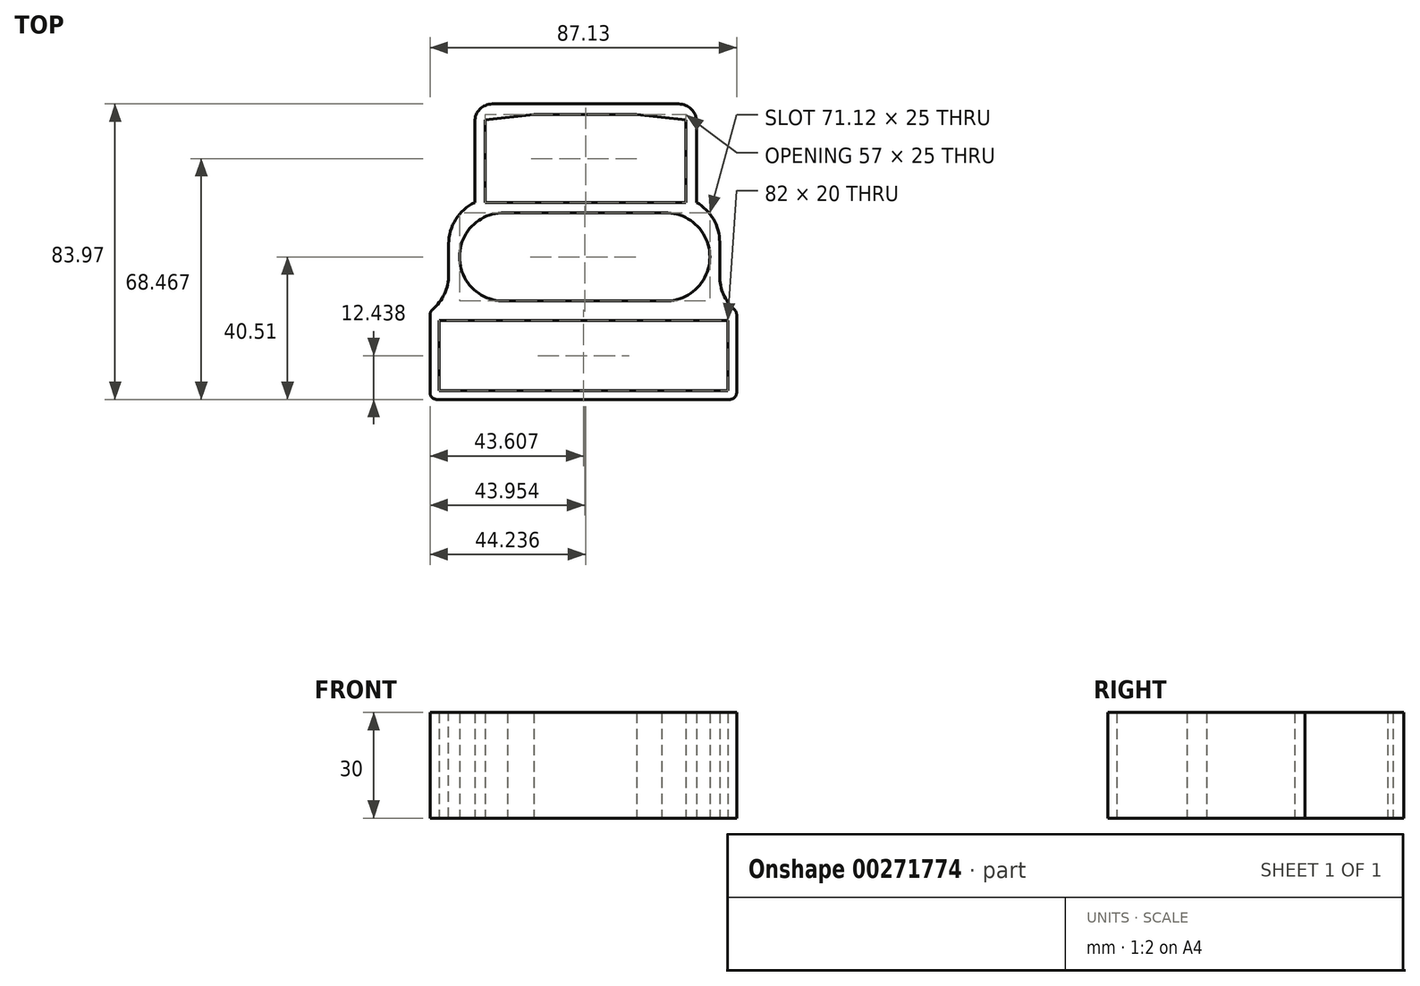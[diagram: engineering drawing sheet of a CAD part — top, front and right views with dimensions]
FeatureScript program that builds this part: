
annotation { "Feature Type Name" : "Feature", "Feature Type Description" : "" }
export const myFeature = defineFeature(function(context is Context, id is Id, definition is map)
    precondition{}
    {
        {
            var Q0;
            Q0=qCreatedBy(makeId("Top.planeOp"),FACE);
            var sketch = newSketch(context, id + "F0", { "sketchPlane" : qUnion([Q0])});
            skLineSegment(sketch, "E0.bottom", {"start": v(-35.62, 12.5) * mm, "end": v(35.38, 12.5) * mm});
            skLineSegment(sketch, "E0.top", {"start": v(-35.62, -12.5) * mm, "end": v(35.38, -12.5) * mm});
            skLineSegment(sketch, "E0.left", {"start": v(-35.62, 12.5) * mm, "end": v(-35.62, -12.5) * mm});
            skLineSegment(sketch, "E0.right", {"start": v(35.38, 12.5) * mm, "end": v(35.38, -12.5) * mm});
            skLineSegment(sketch, "E1.bottom", {"start": v(-38.8, 15.46) * mm, "end": v(38.2, 15.46) * mm});
            skLineSegment(sketch, "E1.top", {"start": v(-38.8, -15.54) * mm, "end": v(38.2, -15.54) * mm});
            skLineSegment(sketch, "E1.left", {"start": v(-38.8, 15.46) * mm, "end": v(-38.8, -15.54) * mm});
            skLineSegment(sketch, "E1.right", {"start": v(38.2, 15.46) * mm, "end": v(38.2, -15.54) * mm});
            skCircle(sketch, "E2", {"center": v(-23.15, 0) * mm, "radius": 12.55 * mm});
            skCircle(sketch, "E3", {"center": v(22.88, 0) * mm, "radius": 12.55 * mm});
            skLineSegment(sketch, "E4.bottom", {"start": v(-28.35, 15.46) * mm, "end": v(28.65, 15.46) * mm});
            skLineSegment(sketch, "E4.top", {"start": v(-28.35, 40.46) * mm, "end": v(28.65, 40.46) * mm});
            skLineSegment(sketch, "E4.left", {"start": v(-28.35, 15.46) * mm, "end": v(-28.35, 40.46) * mm});
            skLineSegment(sketch, "E4.right", {"start": v(28.65, 15.46) * mm, "end": v(28.65, 40.46) * mm});
            skLineSegment(sketch, "E5.bottom", {"start": v(-31.37, 15.46) * mm, "end": v(31.63, 15.46) * mm});
            skLineSegment(sketch, "E5.top", {"start": v(-31.37, 43.46) * mm, "end": v(31.63, 43.46) * mm});
            skLineSegment(sketch, "E5.left", {"start": v(-31.37, 15.46) * mm, "end": v(-31.37, 43.46) * mm});
            skLineSegment(sketch, "E5.right", {"start": v(31.63, 15.46) * mm, "end": v(31.63, 43.46) * mm});
            skLineSegment(sketch, "E6", {"start": v(14.6, 40.46) * mm, "end": v(28.65, 38.9) * mm});
            skLineSegment(sketch, "E7", {"start": v(-14.6, 40.46) * mm, "end": v(-28.35, 38.9) * mm});
            skLineSegment(sketch, "E8.bottom", {"start": v(-41.48, -18.07) * mm, "end": v(40.52, -18.07) * mm});
            skLineSegment(sketch, "E8.top", {"start": v(-41.48, -38.07) * mm, "end": v(40.52, -38.07) * mm});
            skLineSegment(sketch, "E8.left", {"start": v(-41.48, -18.07) * mm, "end": v(-41.48, -38.07) * mm});
            skLineSegment(sketch, "E8.right", {"start": v(40.52, -18.07) * mm, "end": v(40.52, -38.07) * mm});
            skLineSegment(sketch, "E9.bottom", {"start": v(-44.09, -15.54) * mm, "end": v(43.04, -15.54) * mm});
            skLineSegment(sketch, "E9.top", {"start": v(-44.09, -40.5) * mm, "end": v(43.04, -40.5) * mm});
            skLineSegment(sketch, "E9.left", {"start": v(-44.09, -15.54) * mm, "end": v(-44.09, -40.5) * mm});
            skLineSegment(sketch, "E9.right", {"start": v(43.04, -15.54) * mm, "end": v(43.04, -40.5) * mm});
            skSolve(sketch);
        }
        {
            var Q0;
            {var subQ0=sQuery(id+"F0.wireOp",EDGE,"E0.right");var subQ1=sQuery(id+"F0.wireOp",EDGE,"E0.bottom");var subQ2=makeQuery(id+"F0.imprint","INTERSECT",VERTEX,{"derivedFrom":[subQ1,subQ0]});Q0=makeQuery(id+"F0.imprint","IMPRINT",FACE,{"disambiguationData":[TD([[makeQuery(id+"F0.imprint","IMPRINT",EDGE,{"disambiguationData":[TD([[subQ2,1.0]])],"derivedFrom":subQ1}),-1.0]])]});}
            var Q1;
            {var subQ0=sQuery(id+"F0.wireOp",EDGE,"E0.right");var subQ1=sQuery(id+"F0.wireOp",EDGE,"E0.top");var subQ2=makeQuery(id+"F0.imprint","INTERSECT",VERTEX,{"derivedFrom":[subQ1,subQ0]});Q1=makeQuery(id+"F0.imprint","IMPRINT",FACE,{"disambiguationData":[TD([[makeQuery(id+"F0.imprint","IMPRINT",EDGE,{"disambiguationData":[TD([[subQ2,1.0]])],"derivedFrom":subQ1}),1.0]])]});}
            var Q2;
            {var subQ0=sQuery(id+"F0.wireOp",EDGE,"E0.left");var subQ1=sQuery(id+"F0.wireOp",EDGE,"E0.top");var subQ2=makeQuery(id+"F0.imprint","INTERSECT",VERTEX,{"derivedFrom":[subQ1,subQ0]});Q2=makeQuery(id+"F0.imprint","IMPRINT",FACE,{"disambiguationData":[TD([[makeQuery(id+"F0.imprint","IMPRINT",EDGE,{"disambiguationData":[TD([[subQ2,-1.0]])],"derivedFrom":subQ1}),1.0]])]});}
            var Q3;
            {var subQ0=sQuery(id+"F0.wireOp",EDGE,"E0.left");var subQ1=sQuery(id+"F0.wireOp",EDGE,"E0.bottom");var subQ2=makeQuery(id+"F0.imprint","INTERSECT",VERTEX,{"derivedFrom":[subQ1,subQ0]});Q3=makeQuery(id+"F0.imprint","IMPRINT",FACE,{"disambiguationData":[TD([[makeQuery(id+"F0.imprint","IMPRINT",EDGE,{"disambiguationData":[TD([[subQ2,-1.0]])],"derivedFrom":subQ1}),-1.0]])]});}
            var Q4;
            Q4=makeQuery(id+"F0.imprint","IMPRINT",FACE,{"disambiguationData":[TD([[makeQuery(id+"F0.imprint","IMPRINT",EDGE,{"derivedFrom":sQuery(id+"F0.wireOp",EDGE,"E1.bottom")}),-1.0]])]});
            var Q5;
            Q5=makeQuery(id+"F0.imprint","IMPRINT",FACE,{"disambiguationData":[TD([[makeQuery(id+"F0.imprint","IMPRINT",EDGE,{"derivedFrom":sQuery(id+"F0.wireOp",EDGE,"E5.top")}),-1.0]])]});
            var Q6;
            {var subQ3=sQuery(id+"F0.wireOp",EDGE,"E6");Q6=makeQuery(id+"F0.imprint","IMPRINT",FACE,{"disambiguationData":[TD([[makeQuery(id+"F0.imprint","IMPRINT",EDGE,{"derivedFrom":subQ3}),1.0]])]});}
            var Q7;
            {var subQ3=sQuery(id+"F0.wireOp",EDGE,"E7");Q7=makeQuery(id+"F0.imprint","IMPRINT",FACE,{"disambiguationData":[TD([[makeQuery(id+"F0.imprint","IMPRINT",EDGE,{"derivedFrom":subQ3}),-1.0]])]});}
            var Q8;
            Q8=makeQuery(id+"F0.imprint","IMPRINT",FACE,{"disambiguationData":[TD([[makeQuery(id+"F0.imprint","IMPRINT",EDGE,{"derivedFrom":sQuery(id+"F0.wireOp",EDGE,"E8.bottom")}),1.0]])]});
            extrude(context, id + "F1", {"entities" : qUnion([Q0, Q1, Q2, Q3, Q4, Q5, Q6, Q7, Q8]), "depth" : 30 * mm});
        }
        {
            var Q0;
            Q0=makeQuery(id+"F1.opExtrude","SWEPT_EDGE",EDGE,{"disambiguationData":[OSD([sQuery(id+"F0.wireOp",EDGE,"E1.top"),sQuery(id+"F0.wireOp",EDGE,"E1.left")])]});
            var Q1;
            Q1=makeQuery(id+"F1.opExtrude","SWEPT_EDGE",EDGE,{"disambiguationData":[OSD([sQuery(id+"F0.wireOp",EDGE,"E1.bottom"),sQuery(id+"F0.wireOp",EDGE,"E1.left")])]});
            var Q2;
            Q2=makeQuery(id+"F1.opExtrude","SWEPT_EDGE",EDGE,{"disambiguationData":[OSD([sQuery(id+"F0.wireOp",EDGE,"E1.top"),sQuery(id+"F0.wireOp",EDGE,"E1.right")])]});
            var Q3;
            Q3=makeQuery(id+"F1.opExtrude","SWEPT_EDGE",EDGE,{"disambiguationData":[OSD([sQuery(id+"F0.wireOp",EDGE,"E1.bottom"),sQuery(id+"F0.wireOp",EDGE,"E1.right")])]});
            fillet(context, id + "F2", {"entities" : qUnion([Q0, Q1, Q2, Q3]), "radius" : 13 * mm, "tangentPropagation" : true, "allowEdgeOverflow" : false});
        }
        {
            var Q0;
            Q0=makeQuery(id+"F1.opExtrude","SWEPT_EDGE",EDGE,{"disambiguationData":[OSD([sQuery(id+"F0.wireOp",EDGE,"E5.top"),sQuery(id+"F0.wireOp",EDGE,"E5.right")])]});
            var Q1;
            Q1=makeQuery(id+"F1.opExtrude","SWEPT_EDGE",EDGE,{"disambiguationData":[OSD([sQuery(id+"F0.wireOp",EDGE,"E5.top"),sQuery(id+"F0.wireOp",EDGE,"E5.left")])]});
            fillet(context, id + "F3", {"entities" : qUnion([Q0, Q1]), "radius" : 5 * mm, "tangentPropagation" : true, "allowEdgeOverflow" : false});
        }
        {
            var Q0;
            Q0=makeQuery(id+"F2.opFillet","BLEND_EDGE",EDGE,{"blendedFrom":[makeQuery(id+"F1.opExtrude","SWEPT_EDGE",EDGE,{"disambiguationData":[OSD([sQuery(id+"F0.wireOp",EDGE,"E1.left"),sQuery(id+"F0.wireOp",EDGE,"E9.bottom")])]}),makeQuery(id+"F1.opExtrude","SWEPT_FACE",FACE,{"disambiguationData":[OSD([sQuery(id+"F0.wireOp",EDGE,"E9.left")])]})],"blendedInto":[makeQuery(id+"F1.opExtrude","SWEPT_FACE",FACE,{"disambiguationData":[OSD([sQuery(id+"F0.wireOp",EDGE,"E9.left")])]})]});
            var Q1;
            Q1=makeQuery(id+"F1.opExtrude","SWEPT_EDGE",EDGE,{"disambiguationData":[OSD([sQuery(id+"F0.wireOp",EDGE,"E9.top"),sQuery(id+"F0.wireOp",EDGE,"E9.left")])]});
            var Q2;
            Q2=makeQuery(id+"F1.opExtrude","SWEPT_EDGE",EDGE,{"disambiguationData":[OSD([sQuery(id+"F0.wireOp",EDGE,"E9.top"),sQuery(id+"F0.wireOp",EDGE,"E9.right")])]});
            var Q3;
            Q3=makeQuery(id+"F2.opFillet","BLEND_EDGE",EDGE,{"blendedFrom":[makeQuery(id+"F1.opExtrude","SWEPT_EDGE",EDGE,{"disambiguationData":[OSD([sQuery(id+"F0.wireOp",EDGE,"E1.right"),sQuery(id+"F0.wireOp",EDGE,"E9.bottom")])]}),makeQuery(id+"F1.opExtrude","SWEPT_FACE",FACE,{"disambiguationData":[OSD([sQuery(id+"F0.wireOp",EDGE,"E9.right")])]})],"blendedInto":[makeQuery(id+"F1.opExtrude","SWEPT_FACE",FACE,{"disambiguationData":[OSD([sQuery(id+"F0.wireOp",EDGE,"E9.right")])]})]});
            fillet(context, id + "F4", {"entities" : qUnion([Q0, Q1, Q2, Q3]), "radius" : 2 * mm, "tangentPropagation" : true, "allowEdgeOverflow" : false});
        }
    });
